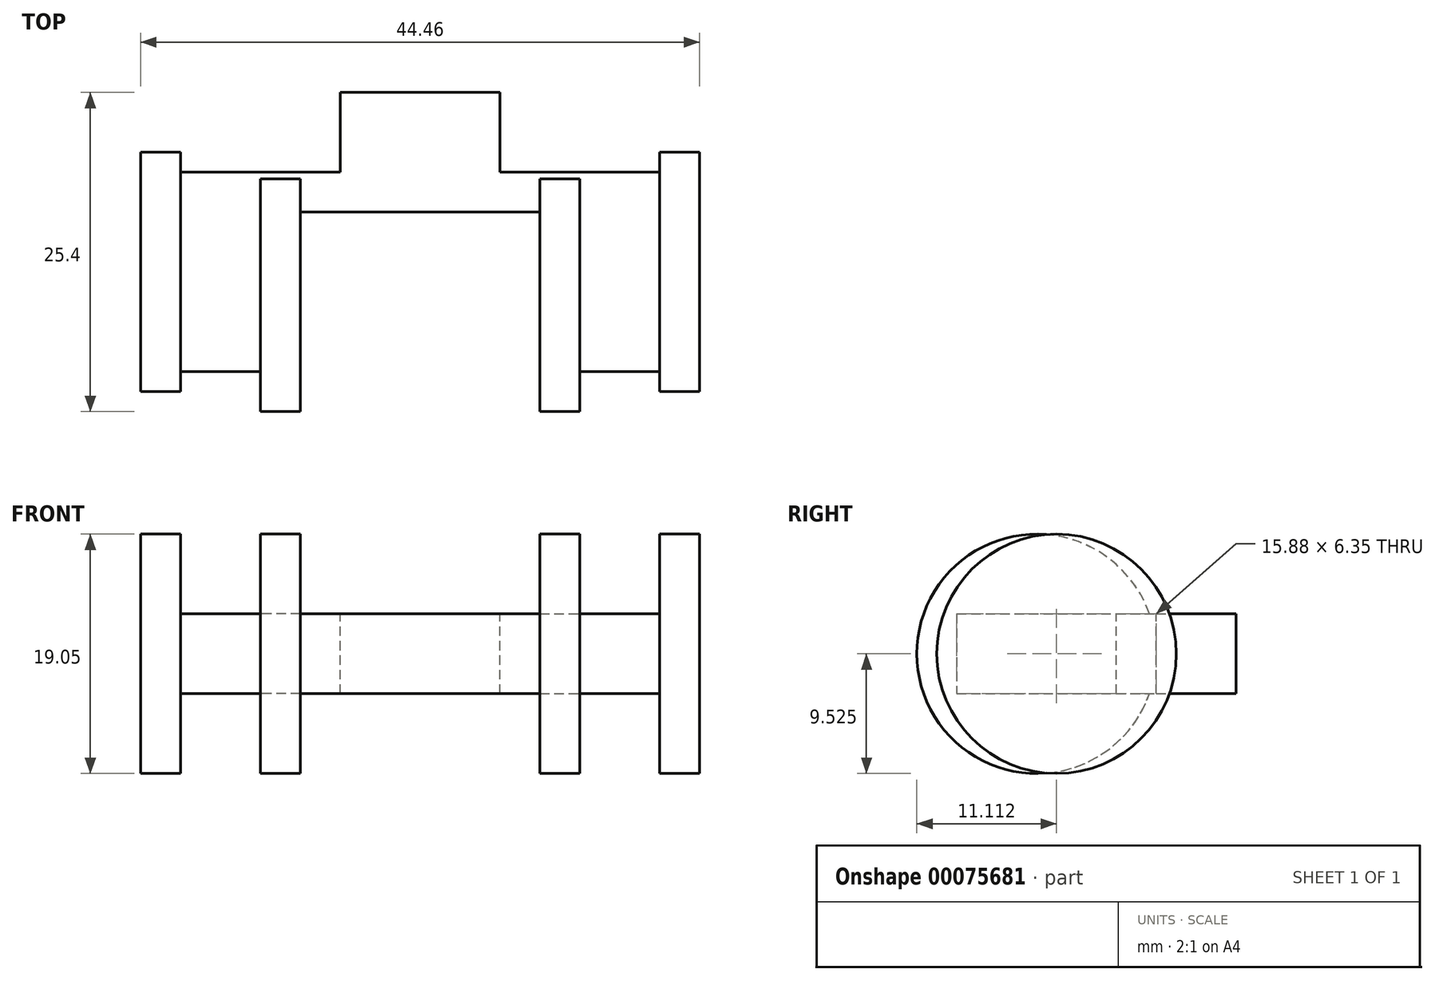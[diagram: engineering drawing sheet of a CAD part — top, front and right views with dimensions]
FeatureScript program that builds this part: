
annotation { "Feature Type Name" : "Feature", "Feature Type Description" : "" }
export const myFeature = defineFeature(function(context is Context, id is Id, definition is map)
    precondition{}
    {
        {
            var Q0;
            Q0=qCreatedBy(makeId("Front.planeOp"),FACE);
            var sketch = newSketch(context, id + "F0", { "sketchPlane" : qUnion([Q0])});
            skLineSegment(sketch, "E0.bottom", {"start": v(0, 0) * mm, "end": v(12.7, 0) * mm});
            skLineSegment(sketch, "E0.top", {"start": v(0, 6.35) * mm, "end": v(12.7, 6.35) * mm});
            skLineSegment(sketch, "E0.left", {"start": v(0, 0) * mm, "end": v(0, 6.35) * mm});
            skLineSegment(sketch, "E0.right", {"start": v(12.7, 0) * mm, "end": v(12.7, 6.35) * mm});
            skSolve(sketch);
        }
        {
            var Q0;
            Q0 = qSketchRegion(id + "F0", true);
            extrude(context, id + "F1", {"entities" : qUnion([Q0]), "depth" : 6.35 * mm});
        }
        {
            var Q0;
            Q0=makeQuery(id+"F1.opExtrude","CAP_FACE",FACE,{"disambiguationData":[OSD([sQuery(id+"F0.wireOp",EDGE,"E0.bottom"),sQuery(id+"F0.wireOp",EDGE,"E0.top"),sQuery(id+"F0.wireOp",EDGE,"E0.left"),sQuery(id+"F0.wireOp",EDGE,"E0.right")])],"isStart":false});
            var sketch = newSketch(context, id + "F2", { "sketchPlane" : qUnion([Q0])});
            skLineSegment(sketch, "E1", {"start": v(-12.7, 0) * mm, "end": v(25.4, 0) * mm});
            skLineSegment(sketch, "E2", {"start": v(25.4, 0) * mm, "end": v(25.4, 6.35) * mm});
            skLineSegment(sketch, "E3", {"start": v(0, 6.35) * mm, "end": v(-12.7, 6.35) * mm});
            skLineSegment(sketch, "E4", {"start": v(12.7, 6.35) * mm, "end": v(25.4, 6.35) * mm});
            skLineSegment(sketch, "E5", {"start": v(-12.7, 6.35) * mm, "end": v(-12.7, 0) * mm});
            skSolve(sketch);
        }
        {
            var Q0;
            Q0 = qSketchRegion(id + "F2", true);
            var Q1;
            Q1=makeQuery(id+"F2.imprint","IMPRINT",FACE,{"disambiguationData":[TD([[makeQuery(id+"F2.imprint","IMPRINT",EDGE,{"derivedFrom":sQuery(id+"F2.wireOp",EDGE,"E3")}),1.0]])]});
            var Q2;
            Q2=makeQuery(id+"F2.imprint","IMPRINT",FACE,{"disambiguationData":[TD([[makeQuery(id+"F2.imprint","IMPRINT",EDGE,{"derivedFrom":makeQuery(id+"F1.opExtrude","CAP_EDGE",EDGE,{"disambiguationData":[OSD([sQuery(id+"F0.wireOp",EDGE,"E0.top")])],"isStart":false})}),-1.0]])]});
            var Q3;
            {var subQ2=sQuery(id+"F2.wireOp",EDGE,"E2");Q3=makeQuery(id+"F2.imprint","IMPRINT",FACE,{"disambiguationData":[TD([[makeQuery(id+"F2.imprint","IMPRINT",EDGE,{"derivedFrom":subQ2}),1.0]])]});}
            extrude(context, id + "F3", {"entities" : qUnion([Q0, Q1, Q2, Q3]), "operationType" : NewBodyOperationType.ADD, "depth" : 3.17 * mm});
        }
        {
            var Q0;
            Q0=makeQuery(id+"F3.opExtrude","CAP_FACE",FACE,{"disambiguationData":[OSD([sQuery(id+"F0.wireOp",EDGE,"E0.top"),sQuery(id+"F2.wireOp",EDGE,"E1"),sQuery(id+"F2.wireOp",EDGE,"E2"),sQuery(id+"F2.wireOp",EDGE,"E3"),sQuery(id+"F2.wireOp",EDGE,"E4"),sQuery(id+"F2.wireOp",EDGE,"E5")])],"isStart":false});
            var sketch = newSketch(context, id + "F4", { "sketchPlane" : qUnion([Q0])});
            skLineSegment(sketch, "E6", {"start": v(-12.7, 6.35) * mm, "end": v(-6.35, 6.35) * mm});
            skLineSegment(sketch, "E7", {"start": v(-6.35, 6.35) * mm, "end": v(-6.35, 0) * mm});
            skLineSegment(sketch, "E8", {"start": v(-6.35, 0) * mm, "end": v(-12.7, 0) * mm});
            skLineSegment(sketch, "E9", {"start": v(-12.7, 0) * mm, "end": v(-12.7, 6.35) * mm});
            skLineSegment(sketch, "E10", {"start": v(25.4, 6.35) * mm, "end": v(19.05, 6.35) * mm});
            skLineSegment(sketch, "E11", {"start": v(19.05, 6.35) * mm, "end": v(19.05, 0) * mm});
            skLineSegment(sketch, "E12", {"start": v(19.05, 0) * mm, "end": v(25.4, 0) * mm});
            skLineSegment(sketch, "E13", {"start": v(25.4, 0) * mm, "end": v(25.4, 6.35) * mm});
            skSolve(sketch);
        }
        {
            var Q0;
            Q0 = qSketchRegion(id + "F4", true);
            var Q1;
            Q1=makeQuery(id+"F4.imprint","IMPRINT",FACE,{"disambiguationData":[TD([[makeQuery(id+"F4.imprint","IMPRINT",EDGE,{"derivedFrom":sQuery(id+"F4.wireOp",EDGE,"E6")}),1.0]])]});
            extrude(context, id + "F5", {"entities" : qUnion([Q0, Q1]), "operationType" : NewBodyOperationType.ADD, "depth" : 12.7 * mm});
        }
        {
            var Q0;
            Q0=makeQuery(id+"F5.boolean.opBoolean","MERGE",FACE,{"derivedFrom":[makeQuery(id+"F3.opExtrude","SWEPT_FACE",FACE,{"disambiguationData":[OSD([sQuery(id+"F2.wireOp",EDGE,"E2")])]}),makeQuery(id+"F5.opExtrude","SWEPT_FACE",FACE,{"disambiguationData":[OSD([sQuery(id+"F4.wireOp",EDGE,"E13")])]})]});
            var sketch = newSketch(context, id + "F6", { "sketchPlane" : qUnion([Q0])});
            skCircle(sketch, "E14", {"center": v(-14.29, 3.18) * mm, "radius": 9.53 * mm});
            skPoint(sketch, "E14.centerSnap0", {"position": v(-22.23, 3.18) * mm});
            skPoint(sketch, "E14.centerSnap1", {"position": v(-14.29, 0) * mm});
            skSolve(sketch);
        }
        {
            var Q0;
            {var subQ0=sQuery(id+"F6.wireOp",EDGE,"E14");var subQ1=makeQuery(id+"F5.boolean.opBoolean","MERGE",EDGE,{"derivedFrom":[makeQuery(id+"F3.opExtrude","SWEPT_EDGE",EDGE,{"disambiguationData":[OSD([sQuery(id+"F2.wireOp",EDGE,"E1"),sQuery(id+"F2.wireOp",EDGE,"E2")])]}),makeQuery(id+"F5.opExtrude","SWEPT_EDGE",EDGE,{"disambiguationData":[OSD([sQuery(id+"F4.wireOp",EDGE,"E12"),sQuery(id+"F4.wireOp",EDGE,"E13")])]})]});var subQ2=makeQuery(id+"F6.imprint","INTERSECT",VERTEX,{"disambiguationData":[OD(0.0)],"derivedFrom":[subQ1,subQ0]});Q0=makeQuery(id+"F6.imprint","IMPRINT",FACE,{"disambiguationData":[TD([[makeQuery(id+"F6.imprint","IMPRINT",EDGE,{"disambiguationData":[TD([[subQ2,-1.0]])],"derivedFrom":subQ0}),1.0]])]});}
            var Q1;
            {var subQ0=sQuery(id+"F6.wireOp",EDGE,"E14");var subQ1=sQuery(id+"F4.wireOp",EDGE,"E13");var subQ2=sQuery(id+"F2.wireOp",EDGE,"E2");var subQ3=makeQuery(id+"F5.boolean.opBoolean","MERGE",EDGE,{"derivedFrom":[makeQuery(id+"F3.opExtrude","SWEPT_EDGE",EDGE,{"disambiguationData":[OSD([subQ2,sQuery(id+"F2.wireOp",EDGE,"E4")])]}),makeQuery(id+"F5.opExtrude","SWEPT_EDGE",EDGE,{"disambiguationData":[OSD([sQuery(id+"F4.wireOp",EDGE,"E10"),subQ1])]})]});var subQ4=makeQuery(id+"F6.imprint","INTERSECT",VERTEX,{"disambiguationData":[OD(0.0)],"derivedFrom":[subQ3,subQ0]});Q1=makeQuery(id+"F6.imprint","IMPRINT",FACE,{"disambiguationData":[TD([[makeQuery(id+"F6.imprint","IMPRINT",EDGE,{"disambiguationData":[TD([[subQ4,-1.0]])],"derivedFrom":subQ0}),1.0]])]});}
            var Q2;
            {var subQ0=sQuery(id+"F6.wireOp",EDGE,"E14");var subQ1=makeQuery(id+"F5.boolean.opBoolean","MERGE",EDGE,{"derivedFrom":[makeQuery(id+"F3.opExtrude","SWEPT_EDGE",EDGE,{"disambiguationData":[OSD([sQuery(id+"F2.wireOp",EDGE,"E2"),sQuery(id+"F2.wireOp",EDGE,"E4")])]}),makeQuery(id+"F5.opExtrude","SWEPT_EDGE",EDGE,{"disambiguationData":[OSD([sQuery(id+"F4.wireOp",EDGE,"E10"),sQuery(id+"F4.wireOp",EDGE,"E13")])]})]});var subQ2=makeQuery(id+"F6.imprint","INTERSECT",VERTEX,{"disambiguationData":[OD(0.0)],"derivedFrom":[subQ1,subQ0]});Q2=makeQuery(id+"F6.imprint","IMPRINT",FACE,{"disambiguationData":[TD([[makeQuery(id+"F6.imprint","IMPRINT",EDGE,{"disambiguationData":[TD([[subQ2,1.0]])],"derivedFrom":subQ0}),1.0]])]});}
            var Q3;
            {var subQ0=sQuery(id+"F2.wireOp",EDGE,"E2");Q3=makeQuery(id+"F6.imprint","IMPRINT",FACE,{"disambiguationData":[TD([[makeQuery(id+"F6.imprint","IMPRINT",EDGE,{"derivedFrom":makeQuery(id+"F3.opExtrude","CAP_EDGE",EDGE,{"disambiguationData":[OSD([subQ0])],"isStart":true})}),1.0]])]});}
            extrude(context, id + "F7", {"entities" : qUnion([Q0, Q1, Q2, Q3]), "operationType" : NewBodyOperationType.ADD, "depth" : 3.17 * mm});
        }
        {
            var Q0;
            Q0=makeQuery(id+"F5.boolean.opBoolean","MERGE",FACE,{"derivedFrom":[makeQuery(id+"F3.opExtrude","SWEPT_FACE",FACE,{"disambiguationData":[OSD([sQuery(id+"F2.wireOp",EDGE,"E5")])]}),makeQuery(id+"F5.opExtrude","SWEPT_FACE",FACE,{"disambiguationData":[OSD([sQuery(id+"F4.wireOp",EDGE,"E9")])]})]});
            var sketch = newSketch(context, id + "F8", { "sketchPlane" : qUnion([Q0])});
            skCircle(sketch, "E15", {"center": v(14.29, 3.18) * mm, "radius": 9.53 * mm});
            skPoint(sketch, "E15.centerSnap0", {"position": v(22.23, 3.18) * mm});
            skPoint(sketch, "E15.centerSnap1", {"position": v(14.29, 6.35) * mm});
            skSolve(sketch);
        }
        {
            var Q0;
            Q0 = qSketchRegion(id + "F8", true);
            extrude(context, id + "F9", {"entities" : qUnion([Q0]), "operationType" : NewBodyOperationType.ADD, "depth" : 3.17 * mm});
        }
        {
            var Q0;
            Q0=makeQuery(id+"F5.opExtrude","SWEPT_FACE",FACE,{"disambiguationData":[OSD([sQuery(id+"F4.wireOp",EDGE,"E11")])]});
            var sketch = newSketch(context, id + "F10", { "sketchPlane" : qUnion([Q0])});
            skCircle(sketch, "E16", {"center": v(15.88, 3.17) * mm, "radius": 9.53 * mm});
            skPoint(sketch, "E16.centerSnap0", {"position": v(22.23, 3.17) * mm});
            skPoint(sketch, "E16.centerSnap1", {"position": v(15.88, 6.35) * mm});
            skSolve(sketch);
        }
        {
            var Q0;
            Q0 = qSketchRegion(id + "F10", true);
            extrude(context, id + "F11", {"entities" : qUnion([Q0]), "operationType" : NewBodyOperationType.ADD, "depth" : 3.17 * mm});
        }
        {
            var Q0;
            Q0=makeQuery(id+"F5.opExtrude","SWEPT_FACE",FACE,{"disambiguationData":[OSD([sQuery(id+"F4.wireOp",EDGE,"E7")])]});
            var sketch = newSketch(context, id + "F12", { "sketchPlane" : qUnion([Q0])});
            skCircle(sketch, "E17", {"center": v(-15.88, 3.18) * mm, "radius": 9.53 * mm});
            skPoint(sketch, "E17.centerSnap0", {"position": v(-15.88, 6.35) * mm});
            skPoint(sketch, "E17.centerSnap1", {"position": v(-22.23, 3.18) * mm});
            skSolve(sketch);
        }
        {
            var Q0;
            Q0 = qSketchRegion(id + "F12", true);
            extrude(context, id + "F13", {"entities" : qUnion([Q0]), "operationType" : NewBodyOperationType.ADD, "depth" : 3.17 * mm});
        }
    });
